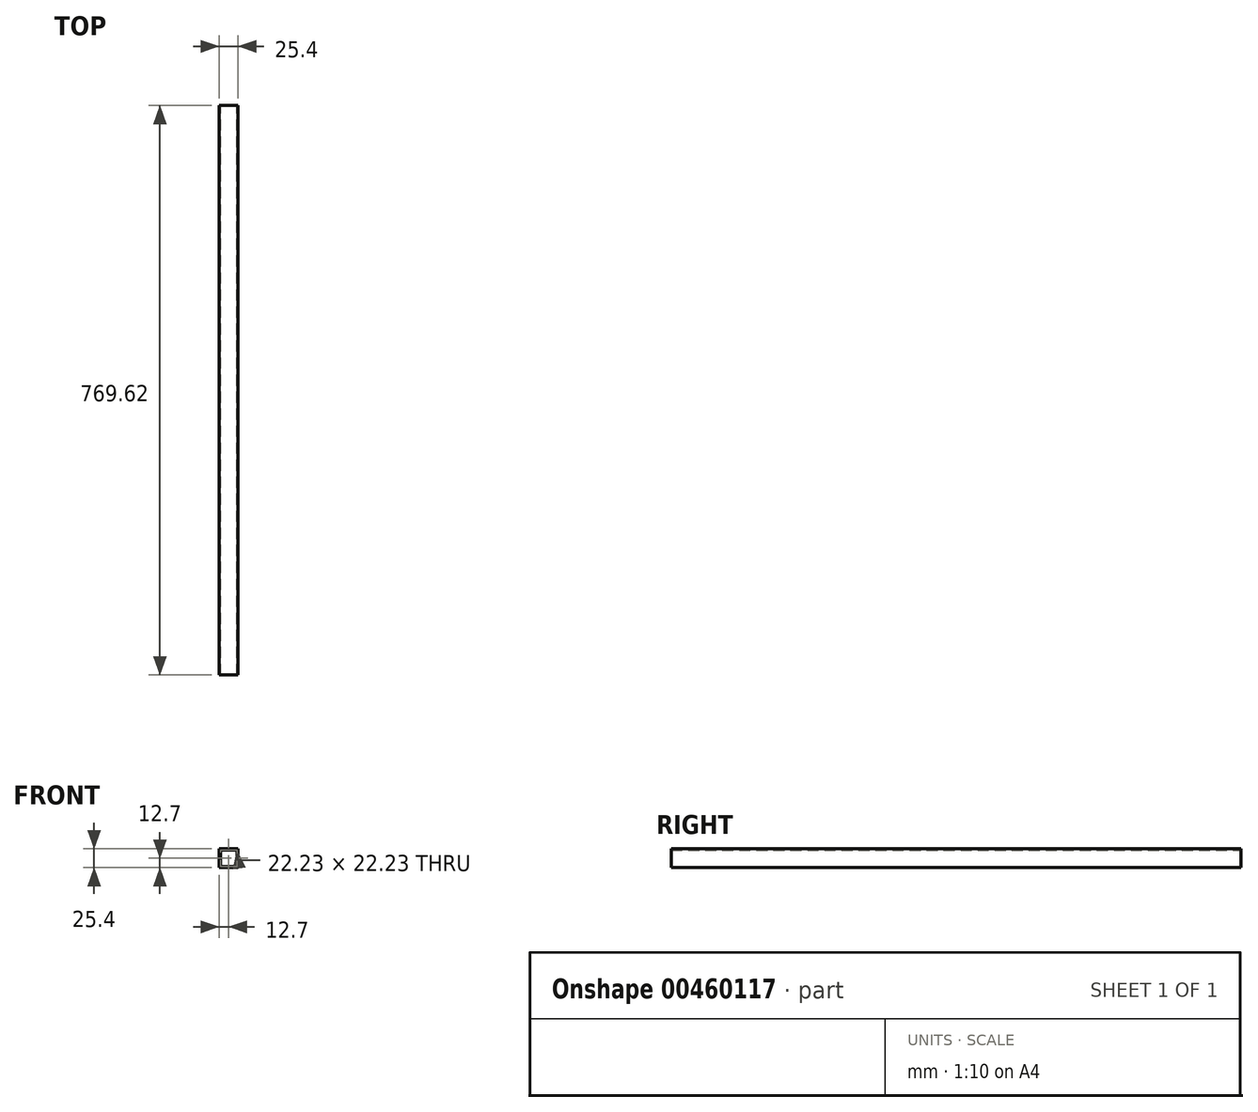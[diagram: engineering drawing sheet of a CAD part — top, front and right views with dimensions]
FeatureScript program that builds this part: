
annotation { "Feature Type Name" : "Feature", "Feature Type Description" : "" }
export const myFeature = defineFeature(function(context is Context, id is Id, definition is map)
    precondition{}
    {
        {
            var Q0;
            Q0=qCreatedBy(makeId("Front.planeOp"),FACE);
            var sketch = newSketch(context, id + "F0", { "sketchPlane" : qUnion([Q0])});
            skLineSegment(sketch, "E0.bottom", {"start": v(12.7, 12.7) * mm, "end": v(-12.7, 12.7) * mm});
            skLineSegment(sketch, "E0.top", {"start": v(12.7, -12.7) * mm, "end": v(-12.7, -12.7) * mm});
            skLineSegment(sketch, "E0.left", {"start": v(12.7, 12.7) * mm, "end": v(12.7, -12.7) * mm});
            skLineSegment(sketch, "E0.right", {"start": v(-12.7, 12.7) * mm, "end": v(-12.7, -12.7) * mm});
            skPoint(sketch, "E0.middle", {"position": v(0, 0) * mm});
            skLineSegment(sketch, "E1.bottom", {"start": v(11.11, 11.11) * mm, "end": v(-11.11, 11.11) * mm});
            skLineSegment(sketch, "E1.top", {"start": v(11.11, -11.11) * mm, "end": v(-11.11, -11.11) * mm});
            skLineSegment(sketch, "E1.left", {"start": v(11.11, 11.11) * mm, "end": v(11.11, -11.11) * mm});
            skLineSegment(sketch, "E1.right", {"start": v(-11.11, 11.11) * mm, "end": v(-11.11, -11.11) * mm});
            skSolve(sketch);
        }
        {
            var Q0;
            Q0=makeQuery(id+"F0.imprint","IMPRINT",FACE,{"disambiguationData":[TD([[makeQuery(id+"F0.imprint","IMPRINT",EDGE,{"derivedFrom":sQuery(id+"F0.wireOp",EDGE,"E0.bottom")}),1.0]])]});
            extrude(context, id + "F1", {"entities" : qUnion([Q0]), "depth" : 769.62 * mm, "offsetDistance" : 25.4 * mm});
        }
    });
